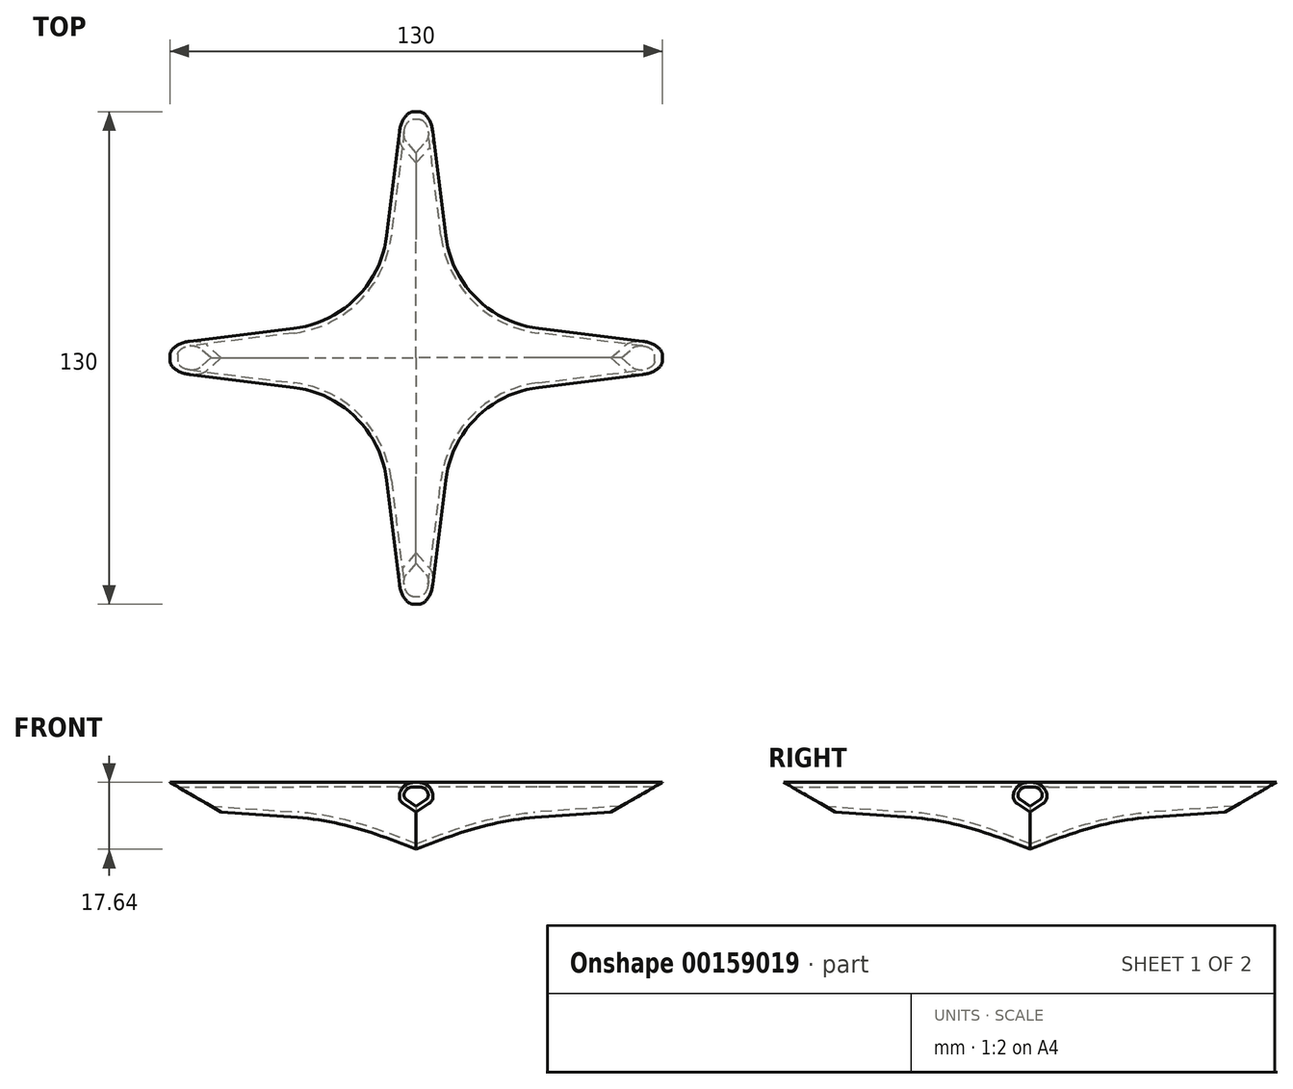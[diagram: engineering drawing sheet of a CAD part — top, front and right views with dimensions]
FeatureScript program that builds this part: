
annotation { "Feature Type Name" : "Feature", "Feature Type Description" : "" }
export const myFeature = defineFeature(function(context is Context, id is Id, definition is map)
    precondition{}
    {
        {
            var Q0;
            Q0=qCreatedBy(makeId("Top.planeOp"),FACE);
            var sketch = newSketch(context, id + "F0", { "sketchPlane" : qUnion([Q0])});
            skLineSegment(sketch, "E0", {"start": v(-15.9, -33.3) * mm, "end": v(-12, -65) * mm});
            skLineSegment(sketch, "E1", {"start": v(-12, -65) * mm, "end": v(12, -65) * mm});
            skLineSegment(sketch, "E2", {"start": v(12, -65) * mm, "end": v(15.9, -33.3) * mm});
            skLineSegment(sketch, "E3", {"start": v(33.3, -15.9) * mm, "end": v(65, -12) * mm});
            skLineSegment(sketch, "E4", {"start": v(65, -12) * mm, "end": v(65, 12) * mm});
            skLineSegment(sketch, "E5", {"start": v(65, 12) * mm, "end": v(33.3, 15.9) * mm});
            skLineSegment(sketch, "E6", {"start": v(15.9, 33.3) * mm, "end": v(12, 65) * mm});
            skLineSegment(sketch, "E7", {"start": v(12, 65) * mm, "end": v(-12, 65) * mm});
            skLineSegment(sketch, "E8", {"start": v(-12, 65) * mm, "end": v(-15.9, 33.3) * mm});
            skLineSegment(sketch, "E9", {"start": v(-33.3, 15.9) * mm, "end": v(-65, 12) * mm});
            skLineSegment(sketch, "E10", {"start": v(-65, 12) * mm, "end": v(-65, -12) * mm});
            skLineSegment(sketch, "E11", {"start": v(-65, -12) * mm, "end": v(-33.3, -15.9) * mm});
            skPoint(sketch, "E12", {"position": v(-65, 0) * mm});
            skPoint(sketch, "E13", {"position": v(0, 65) * mm});
            skPoint(sketch, "E14", {"position": v(65, 0) * mm});
            skPoint(sketch, "E15", {"position": v(0, -65) * mm});
            skLineSegment(sketch, "E16", {"start": v(0, 20) * mm, "end": v(0, -20) * mm, "construction": true});
            skLineSegment(sketch, "E17", {"start": v(-20, 0) * mm, "end": v(20, 0) * mm, "construction": true});
            skPoint(sketch, "E18.visualSharp", {"position": v(17.8, 17.8) * mm});
            skArc(sketch, "E18.filletArc", {"start": v(15.9, 33.3) * mm, "mid": v(21.6, 21.6) * mm, "end": v(33.3, 15.9) * mm});
            skPoint(sketch, "E19.visualSharp", {"position": v(-17.8, 17.8) * mm});
            skArc(sketch, "E19.filletArc", {"start": v(-33.3, 15.9) * mm, "mid": v(-21.6, 21.6) * mm, "end": v(-15.9, 33.3) * mm});
            skPoint(sketch, "E20.visualSharp", {"position": v(-17.8, -17.8) * mm});
            skArc(sketch, "E20.filletArc", {"start": v(-15.9, -33.3) * mm, "mid": v(-21.6, -21.6) * mm, "end": v(-33.3, -15.9) * mm});
            skPoint(sketch, "E21.visualSharp", {"position": v(17.8, -17.8) * mm});
            skArc(sketch, "E21.filletArc", {"start": v(33.3, -15.9) * mm, "mid": v(21.6, -21.6) * mm, "end": v(15.9, -33.3) * mm});
            skSolve(sketch);
        }
        {
            var Q0;
            Q0 = qSketchRegion(id + "F0", true);
            extrude(context, id + "F1", {"entities" : qUnion([Q0]), "oppositeDirection" : true, "depth" : 25 * mm, "hasDraft" : true, "draftAngle" : 60 * degree, "draftPullDirection" : true});
        }
        {
            var Q0;
            Q0=makeQuery(id+"F1.opExtrude","CAP_EDGE",EDGE,{"disambiguationData":[OSD([sQuery(id+"F0.wireOp",EDGE,"E5")])],"isStart":true});
            var Q1;
            Q1=makeQuery(id+"F1.opExtrude","CAP_EDGE",EDGE,{"disambiguationData":[OSD([sQuery(id+"F0.wireOp",EDGE,"E18.filletArc")])],"isStart":true});
            var Q2;
            Q2=makeQuery(id+"F1.opExtrude","CAP_EDGE",EDGE,{"disambiguationData":[OSD([sQuery(id+"F0.wireOp",EDGE,"E6")])],"isStart":true});
            var Q3;
            Q3=makeQuery(id+"F1.opExtrude","CAP_EDGE",EDGE,{"disambiguationData":[OSD([sQuery(id+"F0.wireOp",EDGE,"E8")])],"isStart":true});
            var Q4;
            Q4=makeQuery(id+"F1.opExtrude","CAP_EDGE",EDGE,{"disambiguationData":[OSD([sQuery(id+"F0.wireOp",EDGE,"E11")])],"isStart":true});
            var Q5;
            Q5=makeQuery(id+"F1.opExtrude","CAP_EDGE",EDGE,{"disambiguationData":[OSD([sQuery(id+"F0.wireOp",EDGE,"E2")])],"isStart":true});
            fillet(context, id + "F2", {"entities" : qUnion([Q0, Q1, Q2, Q3, Q4, Q5]), "radius" : 3 * mm, "tangentPropagation" : true, "allowEdgeOverflow" : false});
        }
        {
            var Q0;
            Q0=makeQuery(id+"F1.opExtrude","SWEPT_FACE",FACE,{"disambiguationData":[OSD([sQuery(id+"F0.wireOp",EDGE,"E1")])]});
            var Q1;
            Q1=makeQuery(id+"F1.opExtrude","SWEPT_FACE",FACE,{"disambiguationData":[OSD([sQuery(id+"F0.wireOp",EDGE,"E10")])]});
            var Q2;
            Q2=makeQuery(id+"F1.opExtrude","SWEPT_FACE",FACE,{"disambiguationData":[OSD([sQuery(id+"F0.wireOp",EDGE,"E7")])]});
            var Q3;
            Q3=makeQuery(id+"F1.opExtrude","SWEPT_FACE",FACE,{"disambiguationData":[OSD([sQuery(id+"F0.wireOp",EDGE,"E4")])]});
            shell(context, id + "F3", {"entities" : qUnion([Q0, Q1, Q2, Q3]), "thickness" : 1.2 * mm});
        }
    });
